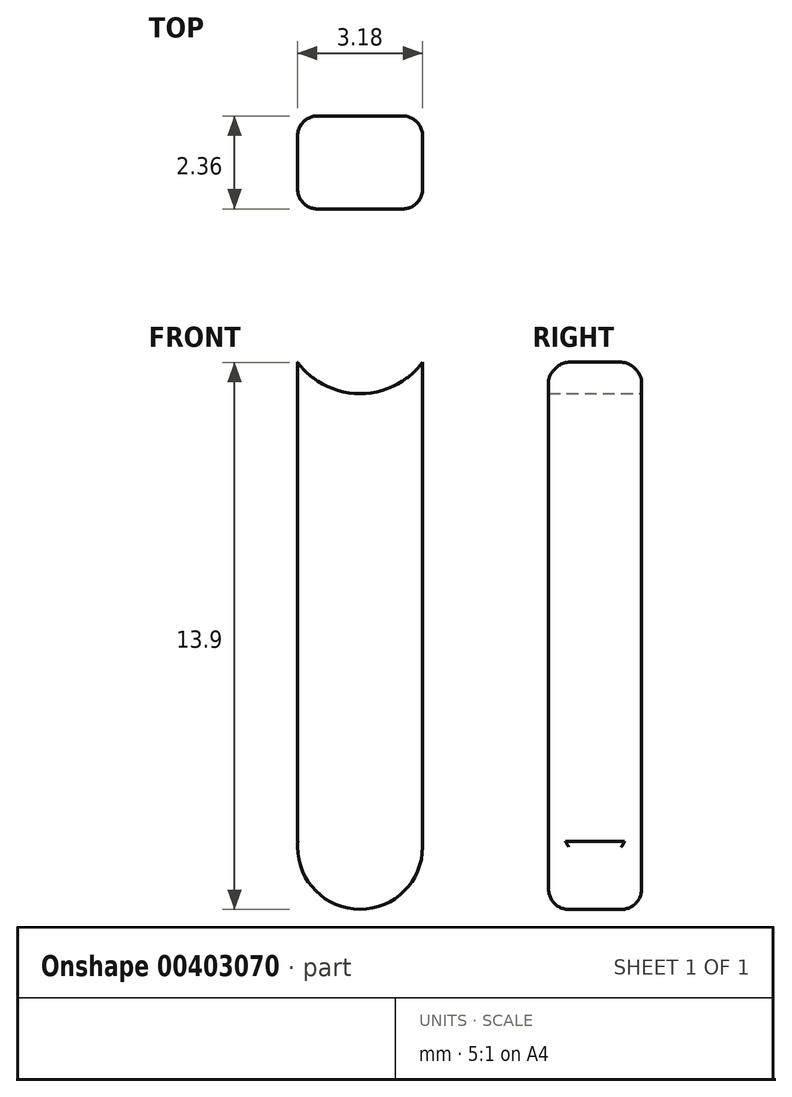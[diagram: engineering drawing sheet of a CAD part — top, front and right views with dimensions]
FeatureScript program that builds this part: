
annotation { "Feature Type Name" : "Feature", "Feature Type Description" : "" }
export const myFeature = defineFeature(function(context is Context, id is Id, definition is map)
    precondition{}
    {
        {
            var Q0;
            Q0=qCreatedBy(makeId("Front.planeOp"),FACE);
            var sketch = newSketch(context, id + "F0", { "sketchPlane" : qUnion([Q0])});
            skArc(sketch, "E0", {"start": v(-1.59, 8.38) * mm, "mid": v(0, 7.59) * mm, "end": v(1.59, 8.38) * mm});
            skLineSegment(sketch, "E1.left", {"start": v(-1.59, -3.79) * mm, "end": v(-1.59, 8.38) * mm});
            skLineSegment(sketch, "E1.right", {"start": v(1.59, -3.79) * mm, "end": v(1.59, 8.38) * mm});
            skArc(sketch, "E2", {"start": v(-1.58, -3.79) * mm, "mid": v(0, -5.52) * mm, "end": v(1.58, -3.79) * mm});
            skLineSegment(sketch, "E3", {"start": v(-1.59, -3.79) * mm, "end": v(-1.58, -3.79) * mm});
            skLineSegment(sketch, "E4.trimOffspring", {"start": v(1.58, -3.79) * mm, "end": v(1.59, -3.79) * mm});
            skSolve(sketch);
        }
        {
            var Q0;
            Q0=makeQuery(id+"F0.imprint","IMPRINT",FACE,{"disambiguationData":[TD([[makeQuery(id+"F0.imprint","IMPRINT",EDGE,{"derivedFrom":sQuery(id+"F0.wireOp",EDGE,"E0")}),-1.0]])]});
            extrude(context, id + "F1", {"entities" : qUnion([Q0]), "endBound" : BoundingType.SYMMETRIC, "depth" : 2.36 * mm});
        }
        {
            var Q0;
            Q0=makeQuery(id+"F1.opExtrude","CAP_EDGE",EDGE,{"disambiguationData":[OSD([sQuery(id+"F0.wireOp",EDGE,"E1.right")])],"isStart":true});
            var Q1;
            Q1=makeQuery(id+"F1.opExtrude","CAP_EDGE",EDGE,{"disambiguationData":[OSD([sQuery(id+"F0.wireOp",EDGE,"E2")])],"isStart":true});
            var Q2;
            Q2=makeQuery(id+"F1.opExtrude","CAP_EDGE",EDGE,{"disambiguationData":[OSD([sQuery(id+"F0.wireOp",EDGE,"E1.left")])],"isStart":true});
            fillet(context, id + "F2", {"entities" : qUnion([Q0, Q1, Q2]), "radius" : 0.5 * mm, "allowEdgeOverflow" : false});
        }
        {
            var Q0;
            Q0=makeQuery(id+"F1.opExtrude","CAP_EDGE",EDGE,{"disambiguationData":[OSD([sQuery(id+"F0.wireOp",EDGE,"E1.left")])],"isStart":false});
            var Q1;
            Q1=makeQuery(id+"F1.opExtrude","CAP_EDGE",EDGE,{"disambiguationData":[OSD([sQuery(id+"F0.wireOp",EDGE,"E2")])],"isStart":false});
            var Q2;
            Q2=makeQuery(id+"F1.opExtrude","CAP_EDGE",EDGE,{"disambiguationData":[OSD([sQuery(id+"F0.wireOp",EDGE,"E1.right")])],"isStart":false});
            fillet(context, id + "F3", {"entities" : qUnion([Q0, Q1, Q2]), "radius" : 0.5 * mm, "allowEdgeOverflow" : false});
        }
    });
